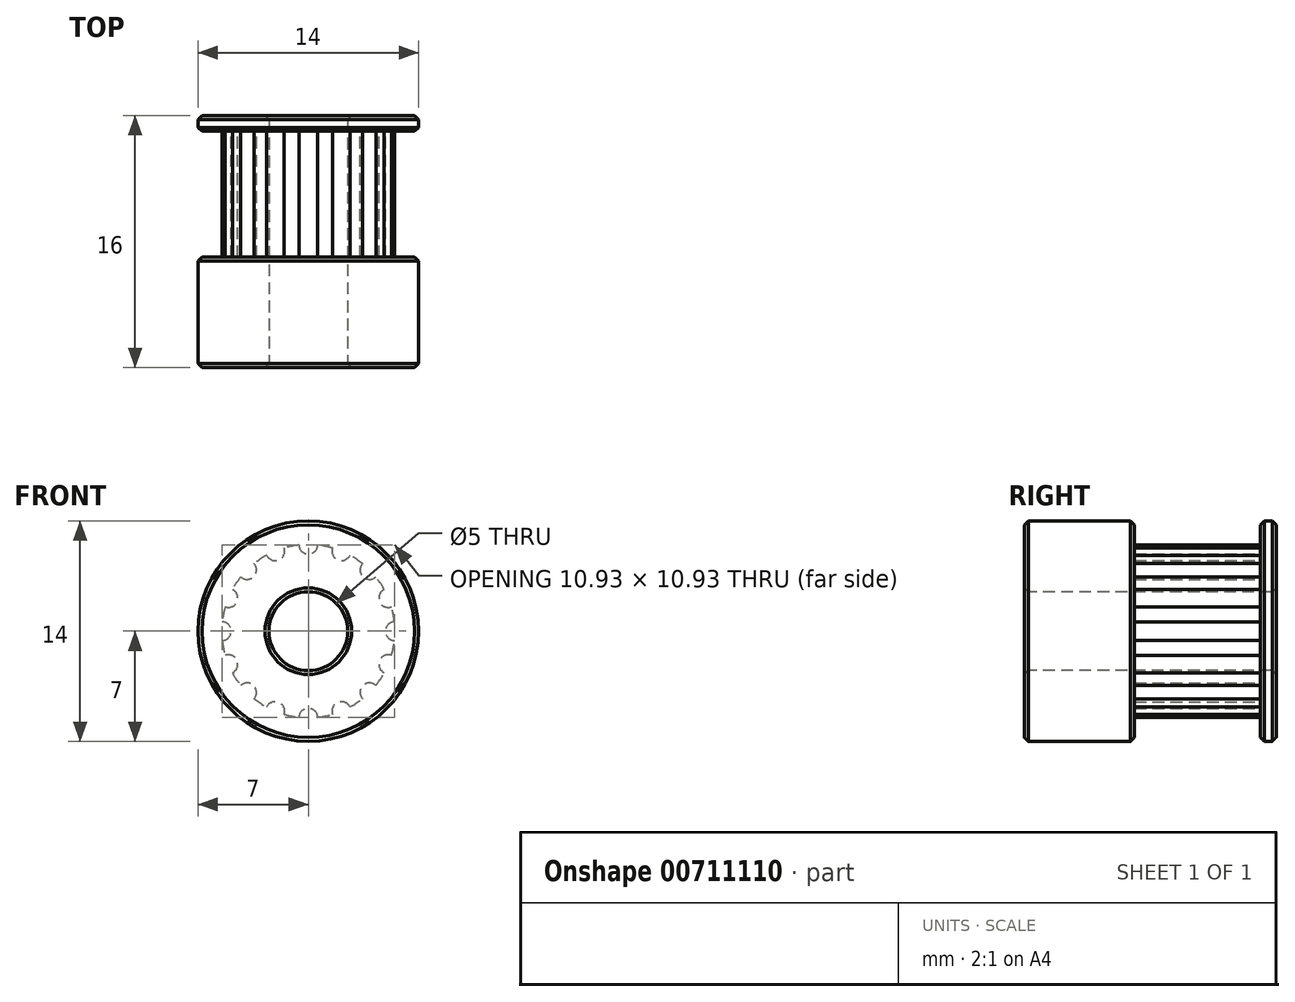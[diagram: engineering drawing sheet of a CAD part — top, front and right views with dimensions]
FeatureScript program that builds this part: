
annotation { "Feature Type Name" : "Feature", "Feature Type Description" : "" }
export const myFeature = defineFeature(function(context is Context, id is Id, definition is map)
    precondition{}
    {
        {
            var Q0;
            Q0=qCreatedBy(makeId("Front.planeOp"),FACE);
            var sketch = newSketch(context, id + "F0", { "sketchPlane" : qUnion([Q0])});
            skCircle(sketch, "E0", {"center": v(0, 0) * mm, "radius": 7 * mm});
            skSolve(sketch);
        }
        {
            var Q0;
            Q0=makeQuery(id+"F0.imprint","IMPRINT",FACE,{"disambiguationData":[TD([[makeQuery(id+"F0.imprint","IMPRINT",EDGE,{"derivedFrom":sQuery(id+"F0.wireOp",EDGE,"E0")}),1.0]])]});
            extrude(context, id + "F1", {"entities" : qUnion([Q0]), "depth" : 1 * mm, "offsetDistance" : 25 * mm});
        }
        {
            var Q0;
            Q0=makeQuery(id+"F1.opExtrude","CAP_FACE",FACE,{"disambiguationData":[OSD([sQuery(id+"F0.wireOp",EDGE,"E0")])],"isStart":false});
            var sketch = newSketch(context, id + "F2", { "sketchPlane" : qUnion([Q0])});
            skCircle(sketch, "E1", {"center": v(0, 0) * mm, "radius": 5.5 * mm});
            skSolve(sketch);
        }
        {
            var Q0;
            Q0=qSketchRegion(id+"F2",true);
            extrude(context, id + "F3", {"entities" : qUnion([Q0]), "operationType" : NewBodyOperationType.ADD, "depth" : 8 * mm, "offsetDistance" : 25 * mm});
        }
        {
            var Q0;
            Q0=makeQuery(id+"F3.opExtrude","CAP_FACE",FACE,{"disambiguationData":[OSD([sQuery(id+"F2.wireOp",EDGE,"E1")])],"isStart":false});
            var sketch = newSketch(context, id + "F4", { "sketchPlane" : qUnion([Q0])});
            skCircle(sketch, "E2", {"center": v(0, 0) * mm, "radius": 7 * mm});
            skSolve(sketch);
        }
        {
            var Q0;
            Q0=qSketchRegion(id+"F4",true);
            extrude(context, id + "F5", {"entities" : qUnion([Q0]), "operationType" : NewBodyOperationType.ADD, "depth" : 7 * mm, "offsetDistance" : 25 * mm});
        }
        {
            var Q0;
            Q0=makeQuery(id+"F1.opExtrude","CAP_FACE",FACE,{"disambiguationData":[OSD([sQuery(id+"F0.wireOp",EDGE,"E0")])],"isStart":false});
            var sketch = newSketch(context, id + "F6", { "sketchPlane" : qUnion([Q0])});
            skCircle(sketch, "E3", {"center": v(0, 0) * mm, "radius": 5 * mm, "construction": true});
            skLineSegment(sketch, "E4", {"start": v(-5.5, 0) * mm, "end": v(0, 0) * mm, "construction": true});
            skLineSegment(sketch, "E5", {"start": v(0, 0) * mm, "end": v(0, 5.5) * mm, "construction": true});
            skCircle(sketch, "E6", {"center": v(0, 5.5) * mm, "radius": 0.6 * mm});
            skCircle(sketch, "E7.1.0", {"center": v(-2.1, 5.08) * mm, "radius": 0.6 * mm});
            skCircle(sketch, "E7.2.0", {"center": v(-3.89, 3.89) * mm, "radius": 0.6 * mm});
            skCircle(sketch, "E7.3.0", {"center": v(-5.08, 2.1) * mm, "radius": 0.6 * mm});
            skCircle(sketch, "E7.4.0", {"center": v(-5.5, 0) * mm, "radius": 0.6 * mm});
            skCircle(sketch, "E7.5.0", {"center": v(-5.08, -2.1) * mm, "radius": 0.6 * mm});
            skCircle(sketch, "E7.6.0", {"center": v(-3.89, -3.89) * mm, "radius": 0.6 * mm});
            skCircle(sketch, "E7.7.0", {"center": v(-2.1, -5.08) * mm, "radius": 0.6 * mm});
            skCircle(sketch, "E7.8.0", {"center": v(0, -5.5) * mm, "radius": 0.6 * mm});
            skCircle(sketch, "E7.9.0", {"center": v(2.1, -5.08) * mm, "radius": 0.6 * mm});
            skCircle(sketch, "E7.10.0", {"center": v(3.89, -3.89) * mm, "radius": 0.6 * mm});
            skCircle(sketch, "E7.11.0", {"center": v(5.08, -2.1) * mm, "radius": 0.6 * mm});
            skCircle(sketch, "E7.12.0", {"center": v(5.5, 0) * mm, "radius": 0.6 * mm});
            skCircle(sketch, "E7.13.0", {"center": v(5.08, 2.1) * mm, "radius": 0.6 * mm});
            skCircle(sketch, "E7.14.0", {"center": v(3.89, 3.89) * mm, "radius": 0.6 * mm});
            skCircle(sketch, "E7.15.0", {"center": v(2.1, 5.08) * mm, "radius": 0.6 * mm});
            skSolve(sketch);
        }
        {
            var Q0;
            Q0=qSketchRegion(id+"F6",true);
            var Q1;
            Q1=makeQuery(id+"F5.opExtrude","CAP_FACE",FACE,{"disambiguationData":[OSD([sQuery(id+"F4.wireOp",EDGE,"E2")])],"isStart":true});
            extrude(context, id + "F7", {"entities" : qUnion([Q0]), "operationType" : NewBodyOperationType.REMOVE, "endBound" : BoundingType.UP_TO_SURFACE, "depth" : 7.5 * mm, "endBoundEntityFace" : qUnion([Q1]), "offsetDistance" : 25 * mm});
        }
        {
            var Q0;
            Q0=makeQuery(id+"F5.opExtrude","CAP_FACE",FACE,{"disambiguationData":[OSD([sQuery(id+"F4.wireOp",EDGE,"E2")])],"isStart":false});
            var sketch = newSketch(context, id + "F8", { "sketchPlane" : qUnion([Q0])});
            skCircle(sketch, "E8", {"center": v(0, 0) * mm, "radius": 2.5 * mm});
            skSolve(sketch);
        }
        {
            var Q0;
            Q0=qSketchRegion(id+"F8",true);
            extrude(context, id + "F9", {"entities" : qUnion([Q0]), "operationType" : NewBodyOperationType.REMOVE, "endBound" : BoundingType.THROUGH_ALL, "oppositeDirection" : true, "depth" : 25 * mm, "offsetDistance" : 25 * mm});
        }
        {
            var Q0;
            Q0=makeQuery(id+"F5.opExtrude","SWEPT_FACE",FACE,{"disambiguationData":[OSD([sQuery(id+"F4.wireOp",EDGE,"E2")])]});
            var Q1;
            Q1=makeQuery(id+"F1.opExtrude","SWEPT_FACE",FACE,{"disambiguationData":[OSD([sQuery(id+"F0.wireOp",EDGE,"E0")])]});
            var Q2;
            Q2=makeQuery(id+"F9.boolean.opBoolean","COPY",FACE,{"derivedFrom":makeQuery(id+"F9.opExtrude","SWEPT_FACE",FACE,{"disambiguationData":[OSD([sQuery(id+"F8.wireOp",EDGE,"E8")])]})});
            chamfer(context, id + "F10", {"entities" : qUnion([Q0, Q1, Q2]), "width" : 0.25 * mm, "tangentPropagation" : true});
        }
    });
